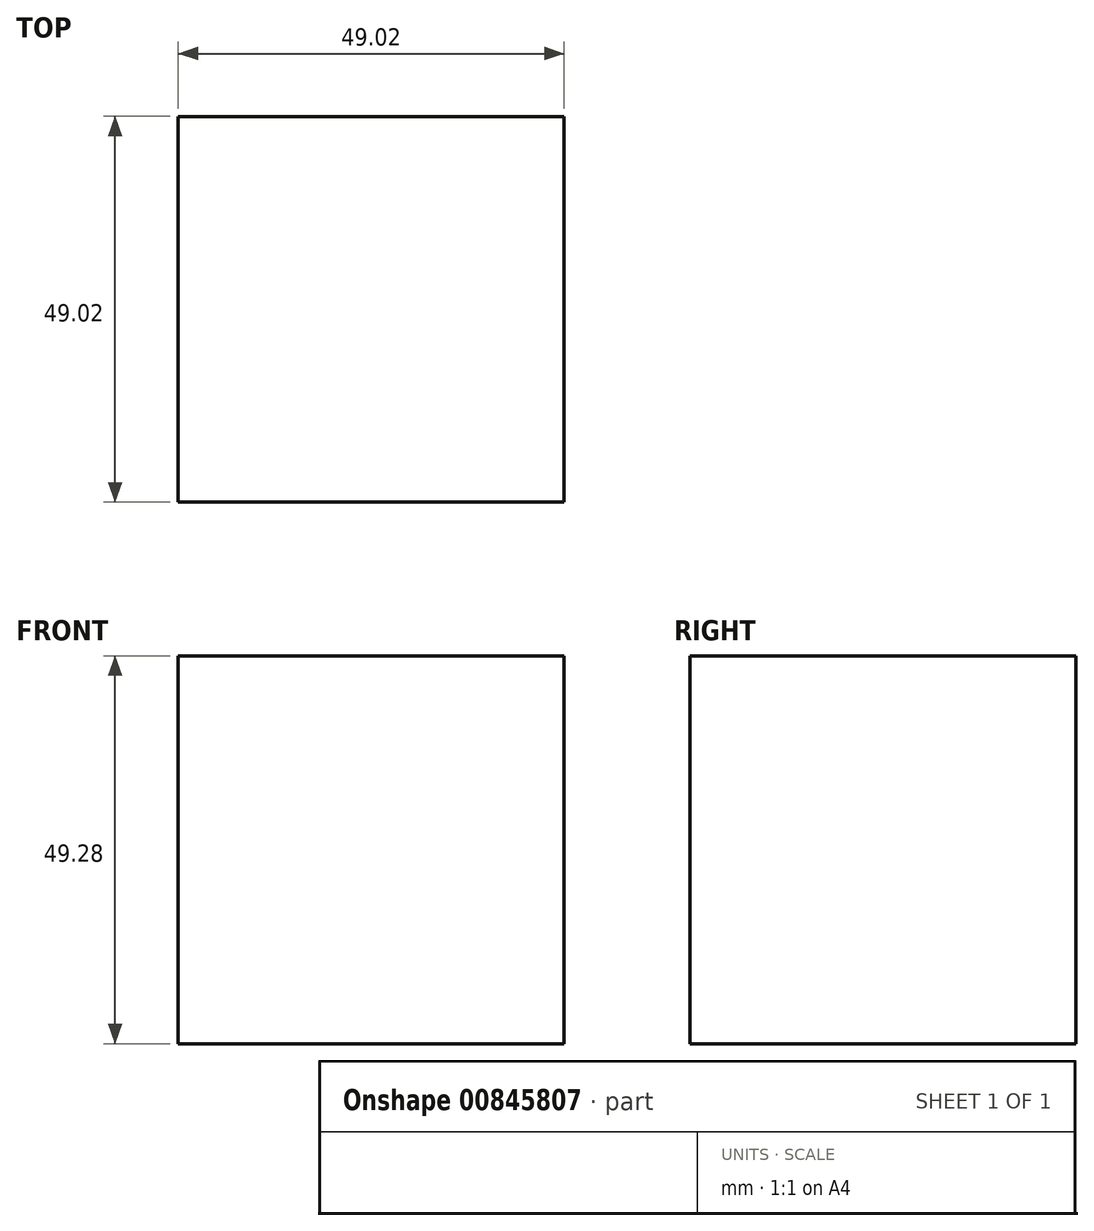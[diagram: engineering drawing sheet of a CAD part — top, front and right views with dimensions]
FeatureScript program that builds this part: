
annotation { "Feature Type Name" : "Feature", "Feature Type Description" : "" }
export const myFeature = defineFeature(function(context is Context, id is Id, definition is map)
    precondition{}
    {
        {
            var Q0;
            Q0=qCreatedBy(makeId("Top.planeOp"),FACE);
            var sketch = newSketch(context, id + "F0", { "sketchPlane" : qUnion([Q0])});
            skLineSegment(sketch, "E0.bottom", {"start": v(-24.5, 24.5) * mm, "end": v(24.5, 24.5) * mm});
            skLineSegment(sketch, "E0.top", {"start": v(-24.5, -24.5) * mm, "end": v(24.5, -24.5) * mm});
            skLineSegment(sketch, "E0.left", {"start": v(-24.5, 24.5) * mm, "end": v(-24.5, -24.5) * mm});
            skLineSegment(sketch, "E0.right", {"start": v(24.5, 24.5) * mm, "end": v(24.5, -24.5) * mm});
            skPoint(sketch, "E0.middle", {"position": v(0, 0) * mm});
            skSolve(sketch);
        }
        {
            var Q0;
            Q0=makeQuery(id+"F0.imprint","IMPRINT",FACE,{"disambiguationData":[TD([[makeQuery(id+"F0.imprint","IMPRINT",EDGE,{"derivedFrom":sQuery(id+"F0.wireOp",EDGE,"E0.bottom")}),-1.0]])]});
            extrude(context, id + "F1", {"entities" : qUnion([Q0]), "depth" : 49.28 * mm, "offsetDistance" : 25.4 * mm});
        }
    });
